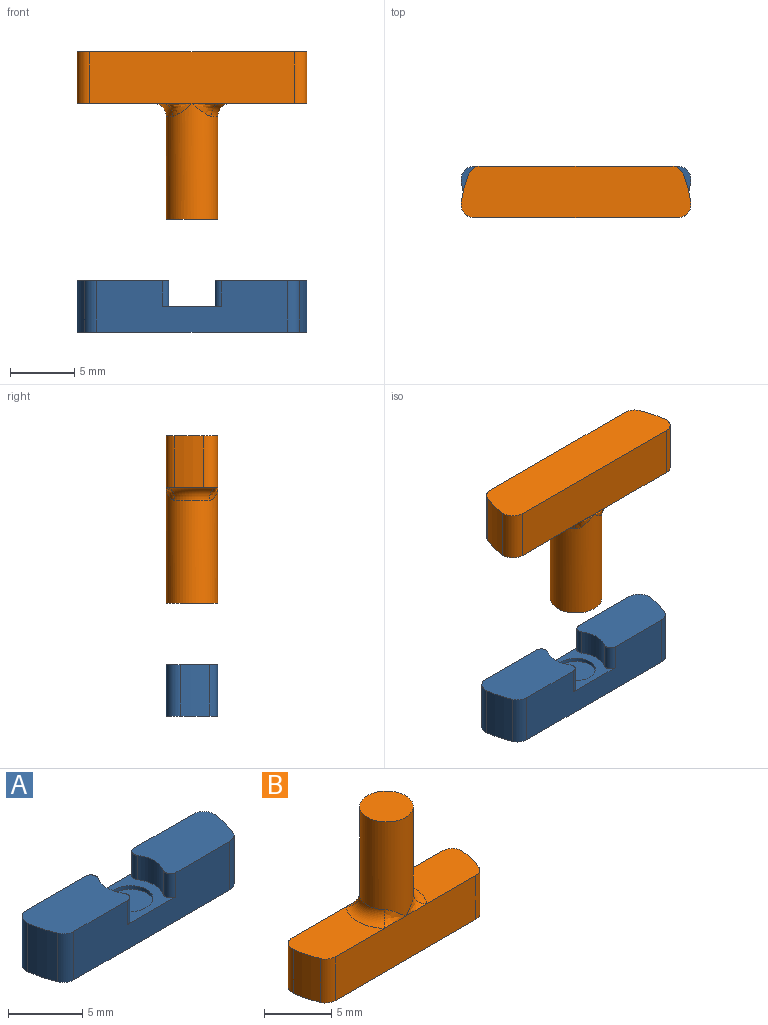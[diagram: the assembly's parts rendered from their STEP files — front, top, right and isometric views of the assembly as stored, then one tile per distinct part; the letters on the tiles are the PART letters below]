
ASSEMBLY  parts=2 mates=1
PART A: 20 faces, bbox 17.9x4x4 mm
  f0: plane 15.87x4mm, normal (0,1,0), area 54.3mm2, adj f1,f5,f6,f9,f11,f12,f15,f16
  f1: plane 7.13x4mm, normal (0,0,1), area 26.3mm2, adj f0,f3,f4,f7,f10,f11,f14,f15
  f2: cylinder r=9mm len=4mm, axis (0,0,-1), area 9.3mm2, adj f5,f6,f12,f13
  f3: plane 14.83x4mm, normal (0,-1,0), area 50.1mm2, adj f1,f5,f6,f9,f10,f13,f14,f17
  f4: cylinder r=9mm len=4mm, axis (0,0,-1), area 9.3mm2, adj f1,f6,f10,f11
  f5: plane 7.13x4mm, normal (0,0,1), area 26.3mm2, adj f0,f2,f3,f8,f12,f13,f16,f17
  f6: plane 17.87x4mm, normal (0,0,-1), area 68.9mm2, adj f0,f2,f3,f4,f10,f11,f12,f13
  f7: cylinder r=2.25mm len=2.45mm, axis (0,0,1), area 5.2mm2, adj f1,f9,f14,f15
  f8: cylinder r=2.25mm len=2.45mm, axis (0,0,1), area 5.2mm2, adj f5,f9,f16,f17
  f9: plane 4.61x4mm, normal (0,0,1), area 9.2mm2, adj f0,f3,f7,f8,f14,f15,f16,f17
  f10: cylinder r=1mm len=4mm, axis (0,0,-1), area 4.7mm2, adj f1,f3,f4,f6
  f11: cylinder r=1mm len=4mm, axis (0,0,-1), area 6.8mm2, adj f0,f1,f4,f6
  f12: cylinder r=1mm len=4mm, axis (0,0,-1), area 6.8mm2, adj f0,f2,f5,f6
  f13: cylinder r=1mm len=4mm, axis (0,0,-1), area 4.7mm2, adj f2,f3,f5,f6
  f14: cylinder r=0.5mm len=2mm, axis (0,0,1), area 2.1mm2, adj f1,f3,f7,f9
  f15: cylinder r=0.5mm len=2mm, axis (0,0,1), area 2.1mm2, adj f0,f1,f7,f9
  f16: cylinder r=0.5mm len=2mm, axis (0,0,1), area 2.1mm2, adj f0,f5,f8,f9
  f17: cylinder r=0.5mm len=2mm, axis (0,0,1), area 2.1mm2, adj f3,f5,f8,f9
  f18: cylinder r=1.5mm len=3mm, axis (0,0,1), area 2.7mm2, adj f9,f19
  f19: plane 3x3mm, normal (0,0,1), area 7.1mm2, adj f18
PART B: 19 faces, bbox 17.9x5.4x13 mm
  f0: plane 6.7x4mm, normal (0,0,1), area 23.4mm2, adj f1,f2,f3,f13,f17,f18
  f1: plane 15.87x4mm, normal (0,1,0), area 63.5mm2, adj f0,f5,f6,f9,f14,f16,f17
  f2: cylinder r=9mm len=4mm, axis (0,0,-1), area 9.3mm2, adj f0,f6,f17,f18
  f3: plane 14.83x4mm, normal (0,-1,0), area 59.3mm2, adj f0,f5,f6,f11,f12,f15,f18
  f4: cylinder r=9mm len=4mm, axis (0,0,-1), area 9.3mm2, adj f5,f6,f15,f16
  f5: plane 6.7x4mm, normal (0,0,1), area 23.4mm2, adj f1,f3,f4,f10,f15,f16
  f6: plane 17.87x4mm, normal (0,0,-1), area 68.9mm2, adj f1,f2,f3,f4,f15,f16,f17,f18
  f7: cylinder r=2mm len=9mm, axis (0,0,-1), area 103.9mm2, adj f8,f9,f10,f11,f12,f13,f14
  f8: plane 4x4mm, normal (0,0,1), area 12.6mm2, adj f7
  f9: bspline ~2.32x1.06mm, area 1.2mm2, adj f1,f7,f10
  f10: torus R=3mm, axis (0,0,1), area 5.4mm2, adj f5,f7,f9,f11
  f11: bspline ~2.32x1.06mm, area 1.2mm2, adj f3,f7,f10
  f12: bspline ~2.32x1.06mm, area 1.2mm2, adj f3,f7,f13
  f13: torus R=3mm, axis (0,0,1), area 5.4mm2, adj f0,f7,f12,f14
  f14: bspline ~2.32x1.06mm, area 1.2mm2, adj f1,f7,f13
  f15: cylinder r=1mm len=4mm, axis (0,0,-1), area 4.7mm2, adj f3,f4,f5,f6
  f16: cylinder r=1mm len=4mm, axis (0,0,-1), area 6.8mm2, adj f1,f4,f5,f6
  f17: cylinder r=1mm len=4mm, axis (0,0,-1), area 6.8mm2, adj f0,f1,f2,f6
  f18: cylinder r=1mm len=4mm, axis (0,0,-1), area 4.7mm2, adj f0,f2,f3,f6
PLACE A t=(5.18,-0.48,-3.4)mm
PLACE B rot(axis=(1,0,0),180deg) t=(5.18,-4.48,18.38)mm
MATE cylindrical B.f7 <-> A.f7  axis (0,0,1) through (5.18,-2.48,9.91)mm
